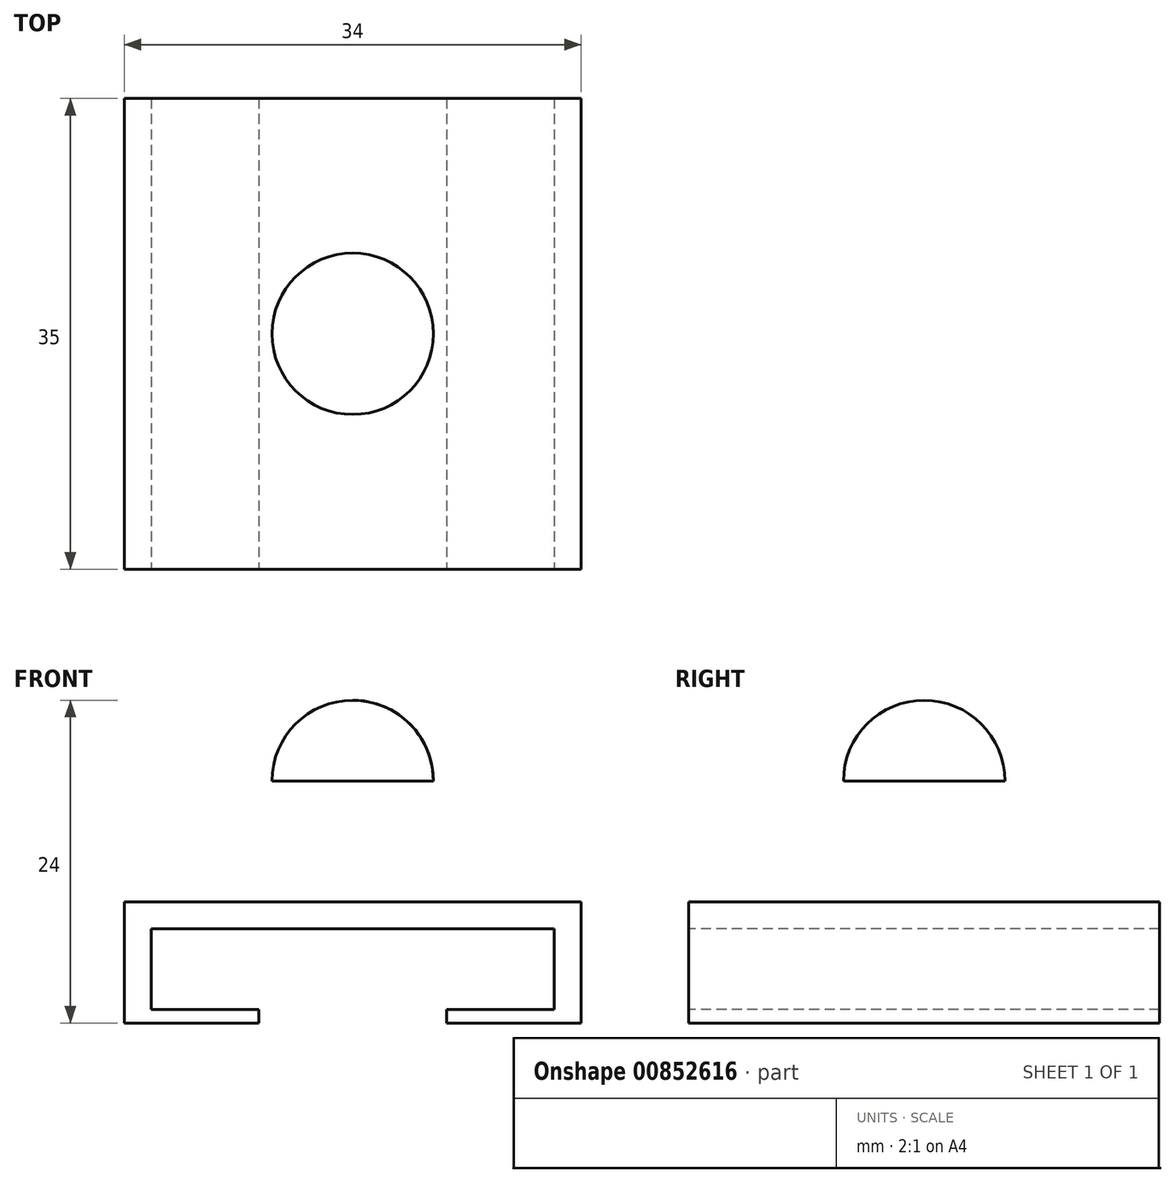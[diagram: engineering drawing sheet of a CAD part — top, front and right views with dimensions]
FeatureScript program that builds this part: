
annotation { "Feature Type Name" : "Feature", "Feature Type Description" : "" }
export const myFeature = defineFeature(function(context is Context, id is Id, definition is map)
    precondition{}
    {
        {
            var Q0;
            Q0=qCreatedBy(makeId("Top.planeOp"),FACE);
            var sketch = newSketch(context, id + "F0", { "sketchPlane" : qUnion([Q0])});
            skLineSegment(sketch, "E0.bottom", {"start": v(17, 17.5) * mm, "end": v(-17, 17.5) * mm});
            skLineSegment(sketch, "E0.top", {"start": v(17, -17.5) * mm, "end": v(-17, -17.5) * mm});
            skLineSegment(sketch, "E0.left", {"start": v(17, 17.5) * mm, "end": v(17, -17.5) * mm});
            skLineSegment(sketch, "E0.right", {"start": v(-17, 17.5) * mm, "end": v(-17, -17.5) * mm});
            skPoint(sketch, "E0.middle", {"position": v(0, 0) * mm});
            skSolve(sketch);
        }
        {
            var Q0;
            Q0=makeQuery(id+"F0.imprint","IMPRINT",FACE,{"disambiguationData":[TD([[makeQuery(id+"F0.imprint","IMPRINT",EDGE,{"derivedFrom":sQuery(id+"F0.wireOp",EDGE,"E0.bottom")}),1.0]])]});
            extrude(context, id + "F1", {"entities" : qUnion([Q0]), "depth" : 9 * mm, "offsetDistance" : 25 * mm});
        }
        {
            var Q0;
            Q0=makeQuery(id+"F1.opExtrude","SWEPT_FACE",FACE,{"disambiguationData":[OSD([sQuery(id+"F0.wireOp",EDGE,"E0.top")])]});
            var sketch = newSketch(context, id + "F2", { "sketchPlane" : qUnion([Q0])});
            skLineSegment(sketch, "E1", {"start": v(-7, 0) * mm, "end": v(-7, 1) * mm});
            skLineSegment(sketch, "E2", {"start": v(-7, 1) * mm, "end": v(-15, 1) * mm});
            skLineSegment(sketch, "E3", {"start": v(-15, 1) * mm, "end": v(-15, 7) * mm});
            skLineSegment(sketch, "E4", {"start": v(-15, 7) * mm, "end": v(0, 7) * mm});
            skLineSegment(sketch, "E5", {"start": v(0, 7) * mm, "end": v(0, 0) * mm});
            skLineSegment(sketch, "E6", {"start": v(0, 0) * mm, "end": v(-7, 0) * mm});
            skLineSegment(sketch, "E7.MirrorCS", {"start": v(0, 0) * mm, "end": v(7, 0) * mm});
            skLineSegment(sketch, "E8.MirrorCS", {"start": v(7, 0) * mm, "end": v(7, 1) * mm});
            skLineSegment(sketch, "E9.MirrorCS", {"start": v(7, 1) * mm, "end": v(15, 1) * mm});
            skLineSegment(sketch, "E10.MirrorCS", {"start": v(15, 1) * mm, "end": v(15, 7) * mm});
            skLineSegment(sketch, "E11.MirrorCS", {"start": v(15, 7) * mm, "end": v(0, 7) * mm});
            skSolve(sketch);
        }
        {
            var Q0;
            Q0=makeQuery(id+"F2.imprint","IMPRINT",FACE,{"disambiguationData":[TD([[makeQuery(id+"F2.imprint","IMPRINT",EDGE,{"derivedFrom":sQuery(id+"F2.wireOp",EDGE,"E1")}),-1.0]])]});
            var Q1;
            Q1=makeQuery(id+"F2.imprint","IMPRINT",FACE,{"disambiguationData":[TD([[makeQuery(id+"F2.imprint","IMPRINT",EDGE,{"derivedFrom":sQuery(id+"F2.wireOp",EDGE,"E5")}),1.0]])]});
            extrude(context, id + "F3", {"entities" : qUnion([Q0, Q1]), "operationType" : NewBodyOperationType.REMOVE, "oppositeDirection" : true, "depth" : 56.95 * mm, "offsetDistance" : 25 * mm});
        }
        {
            var Q0;
            Q0=qCreatedBy(makeId("Front.planeOp"),FACE);
            var sketch = newSketch(context, id + "F4", { "sketchPlane" : qUnion([Q0])});
            skArc(sketch, "E12", {"start": v(6, 18) * mm, "mid": v(4.24, 22.24) * mm, "end": v(0, 24) * mm});
            skLineSegment(sketch, "E13", {"start": v(6, 18) * mm, "end": v(6, 9) * mm});
            skLineSegment(sketch, "E14", {"start": v(6, 9) * mm, "end": v(6, 18) * mm});
            skLineSegment(sketch, "E15", {"start": v(0, 18) * mm, "end": v(6, 18) * mm});
            skLineSegment(sketch, "E16", {"start": v(6, 9) * mm, "end": v(0, 9) * mm});
            skLineSegment(sketch, "E17", {"start": v(0, 9) * mm, "end": v(0, 18) * mm});
            skLineSegment(sketch, "E18", {"start": v(0, 24) * mm, "end": v(0, 18) * mm});
            skSolve(sketch);
        }
        {
            var Q0;
            Q0=qCreatedBy(makeId("Top.planeOp"),FACE);
            var sketch = newSketch(context, id + "F5", { "sketchPlane" : qUnion([Q0])});
            skCircle(sketch, "E19", {"center": v(0, 0) * mm, "radius": 9.97 * mm});
            skSolve(sketch);
        }
        {
            var Q0;
            Q0=makeQuery(id+"F4.imprint","IMPRINT",FACE,{"disambiguationData":[TD([[makeQuery(id+"F4.imprint","IMPRINT",EDGE,{"derivedFrom":sQuery(id+"F4.wireOp",EDGE,"E14")}),1.0]])]});
            var Q1;
            Q1=makeQuery(id+"F4.imprint","IMPRINT",FACE,{"disambiguationData":[TD([[makeQuery(id+"F4.imprint","IMPRINT",EDGE,{"derivedFrom":sQuery(id+"F4.wireOp",EDGE,"E12")}),1.0]])]});
            var Q2;
            Q2=sQuery(id+"F5.wireOp",EDGE,"E19");
            revolve(context, id + "F6", {"operationType" : NewBodyOperationType.ADD, "surfaceOperationType" : NewSurfaceOperationType.NEW, "entities" : qUnion([Q0, Q1]), "axis" : qUnion([Q2]), "revolveType" : RevolveType.FULL});
        }
    });
